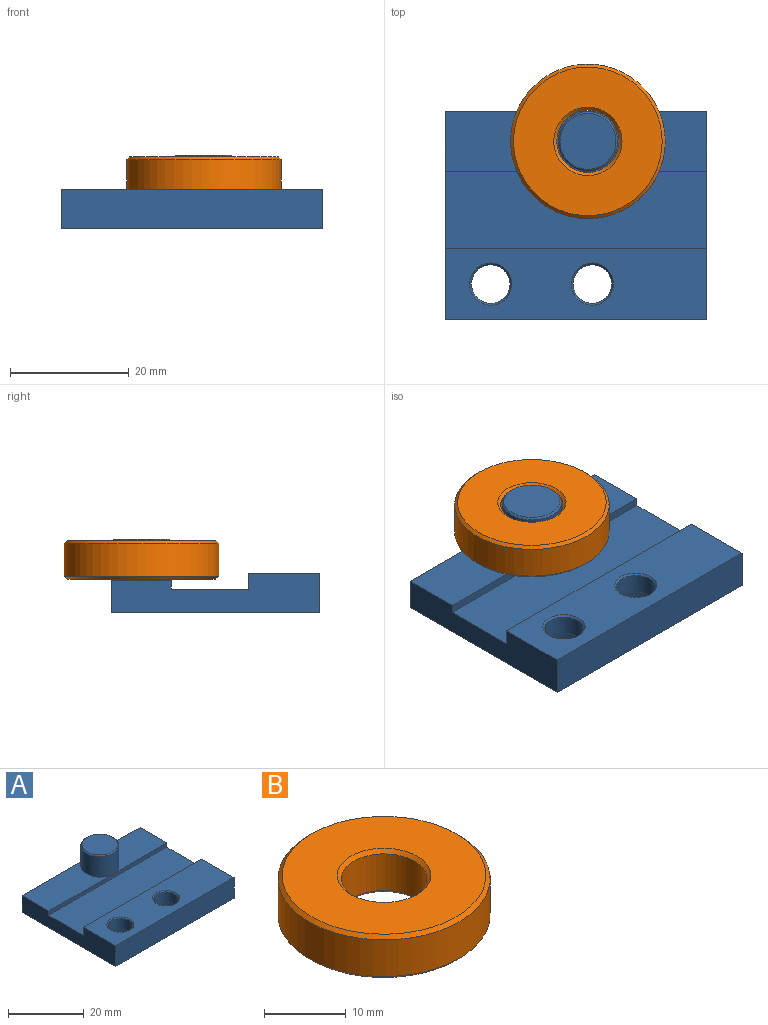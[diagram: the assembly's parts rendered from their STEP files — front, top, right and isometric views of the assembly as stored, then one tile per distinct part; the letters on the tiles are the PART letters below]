
ASSEMBLY  parts=2 mates=1
PART A: 22 faces, bbox 44x35x12.4 mm
  f0: cylinder r=3.25mm len=6.5mm, axis (0,0,1), area 69.4mm2, adj f16,f21
  f1: cylinder r=3.25mm len=6.5mm, axis (0,0,1), area 69.4mm2, adj f15,f19
  f2: plane 20x10mm, normal (0,0,1), area 160.7mm2, adj f4,f6,f11,f13
  f3: plane 44x35mm, normal (0,0,-1), area 1356.8mm2, adj f4,f10,f11,f12,f18,f20
  f4: plane 44x5.4mm, normal (0,1,0), area 237.6mm2, adj f2,f3,f5,f11,f12
  f5: plane 24x10mm, normal (0,0,1), area 200.7mm2, adj f4,f6,f12,f13
  f6: plane 44x1.4mm, normal (0,-1,0), area 61.6mm2, adj f2,f5,f7,f11,f12
  f7: plane 44x13mm, normal (0,0,1), area 572mm2, adj f6,f8,f11,f12
  f8: plane 44x2.7mm, normal (0,1,0), area 118.8mm2, adj f7,f9,f11,f12
  f9: plane 44x12mm, normal (0,0,1), area 448.8mm2, adj f8,f10,f11,f12,f15,f16
  f10: plane 44x6.7mm, normal (0,-1,0), area 294.8mm2, adj f3,f9,f11,f12
  f11: plane 35x6.7mm, normal (1,0,0), area 186.4mm2, adj f2,f3,f4,f6,f7,f8,f9,f10
  f12: plane 35x6.7mm, normal (-1,0,0), area 186.4mm2, adj f3,f4,f5,f6,f7,f8,f9,f10
  f13: cylinder r=5mm len=10mm, axis (0,0,-1), area 210.5mm2, adj f2,f5,f17
  f14: plane 9.4x9.4mm, normal (0,0,1), area 69.4mm2, adj f17
  f15: cone r=3.25mm half-angle=45deg, axis (0,0,1), area 9.1mm2, adj f1,f9
  f16: cone r=3.25mm half-angle=45deg, axis (0,0,1), area 9.1mm2, adj f0,f9
  f17: cone r=4.7mm half-angle=45deg, axis (0,0,-1), area 12.9mm2, adj f13,f14
  f18: cylinder r=5.4mm len=10.8mm, axis (0,0,-1), area 101.8mm2, adj f3,f19
  f19: plane 10.8x10.8mm, normal (0,0,-1), area 58.4mm2, adj f1,f18
  f20: cylinder r=5.4mm len=10.8mm, axis (0,0,-1), area 101.8mm2, adj f3,f21
  f21: plane 10.8x10.8mm, normal (0,0,-1), area 58.4mm2, adj f0,f20
PART B: 8 faces, bbox 26x26x6.5 mm
  f0: cylinder r=5.25mm len=10.5mm, axis (0,0,-1), area 181.4mm2, adj f5,f7
  f1: cylinder r=13mm len=26mm, axis (0,0,-1), area 449.2mm2, adj f4,f6
  f2: plane 25x25mm, normal (0,0,1), area 387mm2, adj f6,f7
  f3: plane 25x25mm, normal (0,0,-1), area 387mm2, adj f4,f5
  f4: cone r=13mm half-angle=45deg, axis (0,0,1), area 56.6mm2, adj f1,f3
  f5: cone r=5.75mm half-angle=45deg, axis (0,0,-1), area 24.4mm2, adj f0,f3
  f6: cone r=12.5mm half-angle=45deg, axis (0,0,-1), area 56.6mm2, adj f1,f2
  f7: cone r=5.25mm half-angle=45deg, axis (0,0,1), area 24.4mm2, adj f0,f2
PLACE A t=(-36.44,-12.86,1.99)mm
PLACE B rot(axis=(-1,0,0),180deg) t=(-12.44,-0.36,14.15)mm
MATE cylindrical B.f0 <-> A.f13  axis (0,0,-1) through (-12.44,-0.36,13.65)mm
